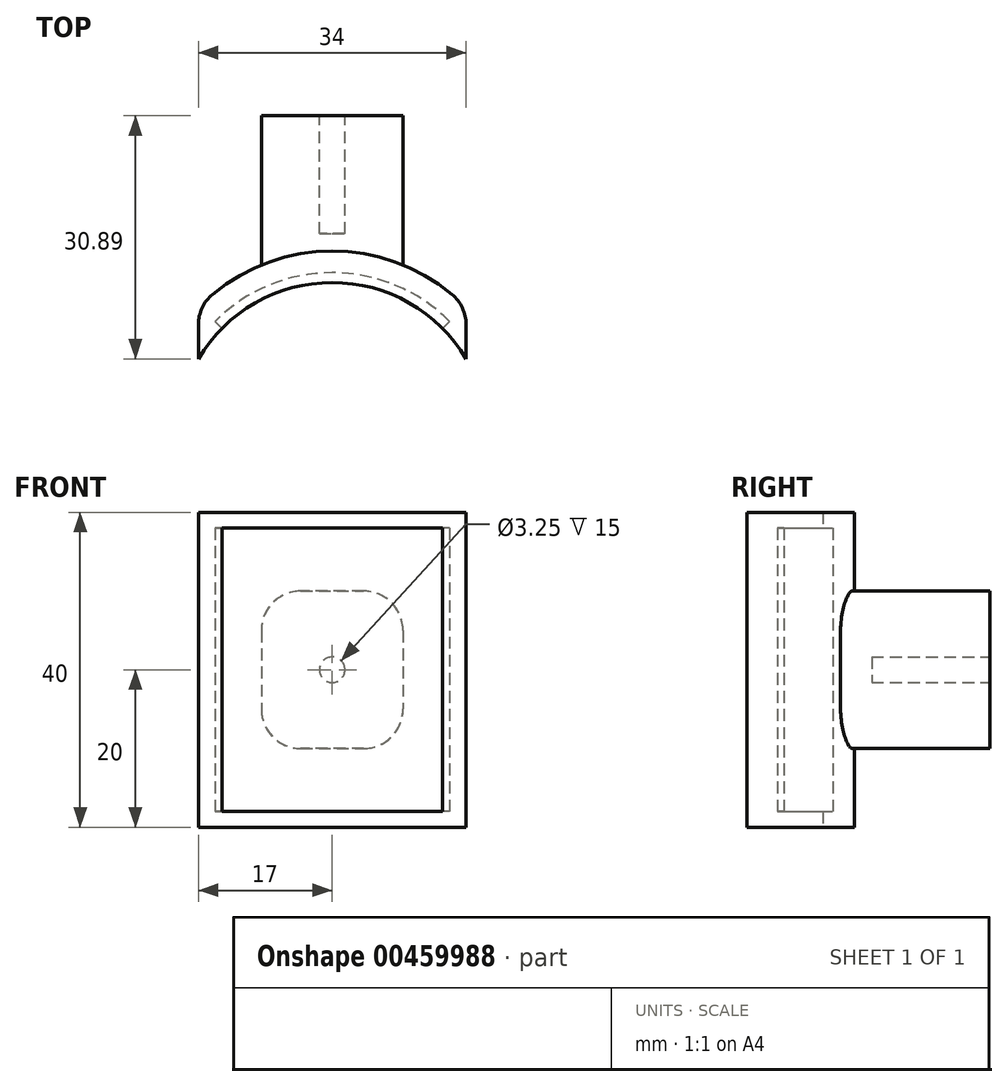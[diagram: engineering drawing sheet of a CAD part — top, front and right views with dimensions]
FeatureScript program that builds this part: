
annotation { "Feature Type Name" : "Feature", "Feature Type Description" : "" }
export const myFeature = defineFeature(function(context is Context, id is Id, definition is map)
    precondition{}
    {
        {
            var Q0;
            Q0=qCreatedBy(makeId("Top.planeOp"),FACE);
            var sketch = newSketch(context, id + "F0", { "sketchPlane" : qUnion([Q0])});
            skArc(sketch, "E0", {"start": v(17, 0) * mm, "mid": v(0, 9.7) * mm, "end": v(-17, 0) * mm});
            skArc(sketch, "E1", {"start": v(15.2, 8.2) * mm, "mid": v(0, 13.7) * mm, "end": v(-15.2, 8.2) * mm});
            skPoint(sketch, "E2", {"position": v(0, 9.7) * mm});
            skLineSegment(sketch, "E3", {"start": v(-17, 0) * mm, "end": v(-17, 4.35) * mm});
            skLineSegment(sketch, "E4", {"start": v(17, 4.35) * mm, "end": v(17, 0) * mm});
            skLineSegment(sketch, "E5", {"start": v(0, 9.7) * mm, "end": v(0, 13.7) * mm, "construction": true});
            skPoint(sketch, "E6.visualSharp", {"position": v(-17, 6.53) * mm});
            skArc(sketch, "E6.filletArc", {"start": v(-15.2, 8.2) * mm, "mid": v(-16.53, 6.48) * mm, "end": v(-17, 4.35) * mm});
            skPoint(sketch, "E7.visualSharp", {"position": v(17, 6.53) * mm});
            skArc(sketch, "E7.filletArc", {"start": v(17, 4.35) * mm, "mid": v(16.53, 6.48) * mm, "end": v(15.2, 8.2) * mm});
            skSolve(sketch);
        }
        {
            var Q0;
            Q0 = qSketchRegion(id + "F0", true);
            extrude(context, id + "F1", {"entities" : qUnion([Q0]), "depth" : 40 * mm});
        }
        {
            var Q0;
            Q0=qCreatedBy(makeId("Top.planeOp"),FACE);
            cPlane(context, id + "F2", {"entities" : qUnion([Q0]), "cplaneType" : CPlaneType.OFFSET, "offset" : 20 * mm, "width" : 150 * mm, "height" : 150 * mm});
        }
        {
            var Q0;
            Q0=qCreatedBy(id+"F2.planeOp",FACE);
            var sketch = newSketch(context, id + "F3", { "sketchPlane" : qUnion([Q0])});
            skLineSegment(sketch, "E8.bottom", {"start": v(-9, 10.89) * mm, "end": v(9, 10.89) * mm});
            skLineSegment(sketch, "E8.top", {"start": v(-9, 30.89) * mm, "end": v(9, 30.89) * mm});
            skLineSegment(sketch, "E8.left", {"start": v(-9, 10.89) * mm, "end": v(-9, 30.89) * mm});
            skLineSegment(sketch, "E8.right", {"start": v(9, 10.89) * mm, "end": v(9, 30.89) * mm});
            skPoint(sketch, "E9", {"position": v(0, 30.89) * mm});
            skLineSegment(sketch, "E10", {"start": v(0, 30.89) * mm, "end": v(0, 0) * mm, "construction": true});
            skPoint(sketch, "E11", {"position": v(0, 10.89) * mm});
            skArc(sketch, "E12", {"start": v(17, 2.18) * mm, "mid": v(0, 10.89) * mm, "end": v(-17, 2.18) * mm, "construction": true});
            skSolve(sketch);
        }
        {
            var Q0;
            Q0 = qSketchRegion(id + "F3", true);
            extrude(context, id + "F4", {"entities" : qUnion([Q0]), "operationType" : NewBodyOperationType.ADD, "depth" : 10 * mm, "hasSecondDirection" : true, "secondDirectionOppositeDirection" : true, "secondDirectionDepth" : 10 * mm});
        }
        {
            var Q0;
            Q0=qCreatedBy(makeId("Top.planeOp"),FACE);
            cPlane(context, id + "F5", {"entities" : qUnion([Q0]), "cplaneType" : CPlaneType.OFFSET, "offset" : 2 * mm, "width" : 150 * mm, "height" : 150 * mm});
        }
        {
            var Q0;
            Q0=qCreatedBy(id+"F5.planeOp",FACE);
            var sketch = newSketch(context, id + "F6", { "sketchPlane" : qUnion([Q0])});
            skLineSegment(sketch, "E13", {"start": v(0, 9.7) * mm, "end": v(0, 9.7) * mm});
            skArc(sketch, "E14", {"start": v(14.89, 4.76) * mm, "mid": v(0, 10.95) * mm, "end": v(-14.89, 4.76) * mm});
            skLineSegment(sketch, "E15", {"start": v(0, 9.7) * mm, "end": v(0, 10.95) * mm, "construction": true});
            skArc(sketch, "E16", {"start": v(14, 3.88) * mm, "mid": v(0, 9.7) * mm, "end": v(-14, 3.88) * mm});
            skLineSegment(sketch, "E17", {"start": v(-14.89, 4.76) * mm, "end": v(-14, 3.88) * mm});
            skLineSegment(sketch, "E18", {"start": v(14.89, 4.76) * mm, "end": v(14, 3.88) * mm});
            skSolve(sketch);
        }
        {
            var Q0;
            Q0 = qSketchRegion(id + "F6", true);
            extrude(context, id + "F7", {"entities" : qUnion([Q0]), "operationType" : NewBodyOperationType.REMOVE, "depth" : 36 * mm});
        }
        {
            var Q0;
            Q0=makeQuery(id+"F4.opExtrude","SWEPT_FACE",FACE,{"disambiguationData":[OSD([sQuery(id+"F3.wireOp",EDGE,"E8.top")])]});
            var sketch = newSketch(context, id + "F8", { "sketchPlane" : qUnion([Q0])});
            skCircle(sketch, "E19", {"center": v(0, 20) * mm, "radius": 1.63 * mm});
            skPoint(sketch, "E19.centerSnap0", {"position": v(9, 20) * mm});
            skSolve(sketch);
        }
        {
            var Q0;
            Q0 = qSketchRegion(id + "F8", true);
            extrude(context, id + "F9", {"entities" : qUnion([Q0]), "operationType" : NewBodyOperationType.REMOVE, "oppositeDirection" : true, "depth" : 15 * mm});
        }
        {
            var Q0;
            Q0=makeQuery(id+"F4.opExtrude","CAP_EDGE",EDGE,{"disambiguationData":[OSD([sQuery(id+"F3.wireOp",EDGE,"E8.right")])],"isStart":false});
            var Q1;
            Q1=makeQuery(id+"F4.opExtrude","CAP_EDGE",EDGE,{"disambiguationData":[OSD([sQuery(id+"F3.wireOp",EDGE,"E8.left")])],"isStart":false});
            var Q2;
            Q2=makeQuery(id+"F4.opExtrude","CAP_EDGE",EDGE,{"disambiguationData":[OSD([sQuery(id+"F3.wireOp",EDGE,"E8.left")])],"isStart":true});
            var Q3;
            Q3=makeQuery(id+"F4.opExtrude","CAP_EDGE",EDGE,{"disambiguationData":[OSD([sQuery(id+"F3.wireOp",EDGE,"E8.right")])],"isStart":true});
            fillet(context, id + "F10", {"entities" : qUnion([Q0, Q1, Q2, Q3]), "radius" : 5 * mm, "tangentPropagation" : true, "allowEdgeOverflow" : false});
        }
    });
